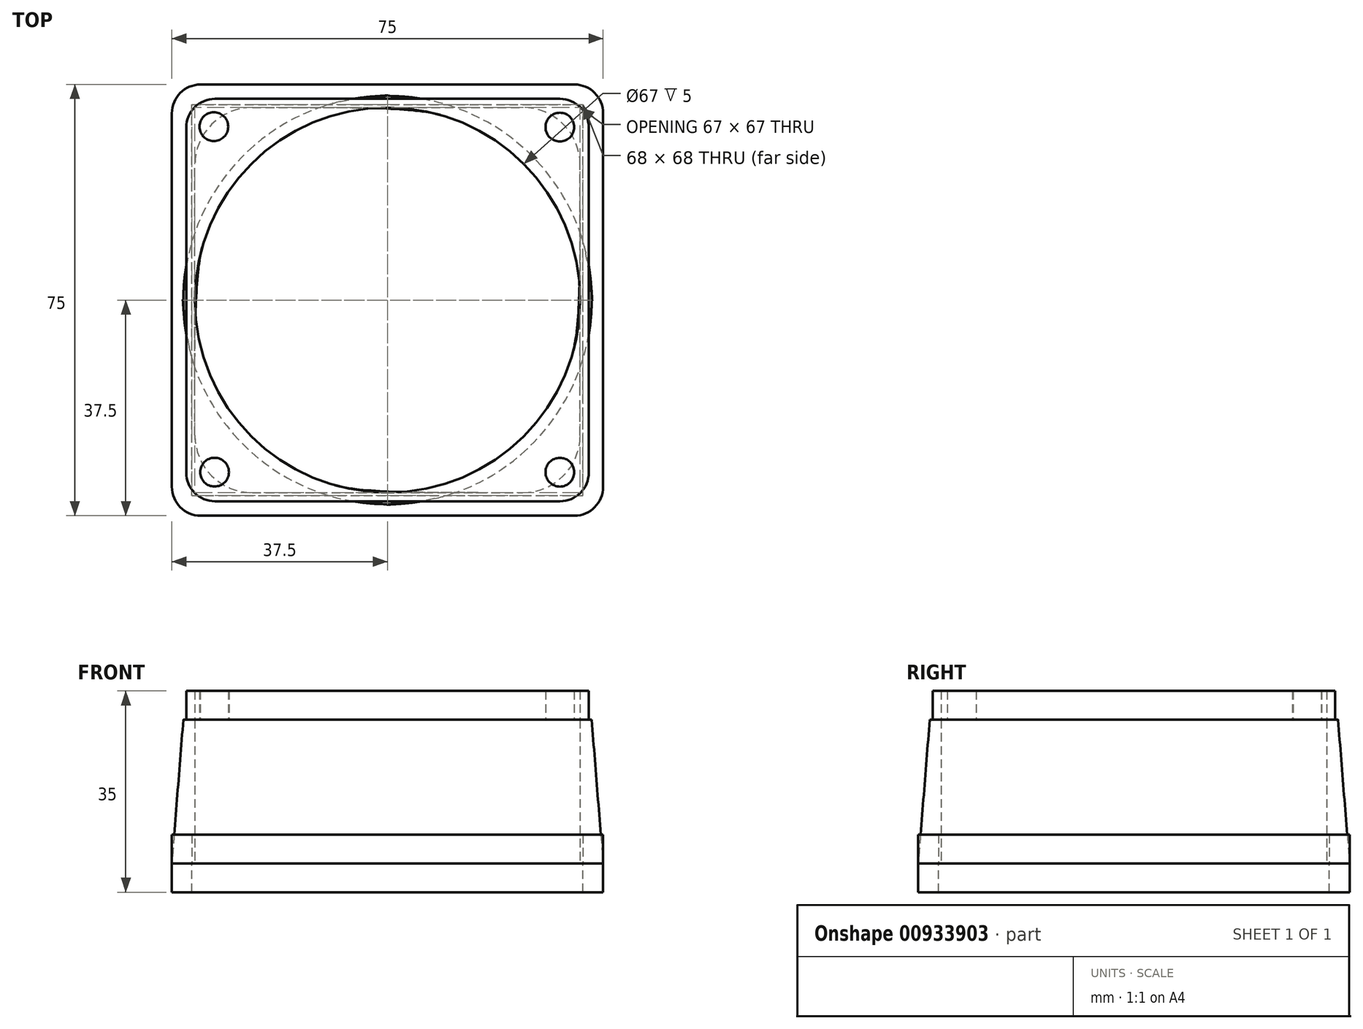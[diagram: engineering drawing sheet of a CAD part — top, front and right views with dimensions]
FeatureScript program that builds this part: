
annotation { "Feature Type Name" : "Feature", "Feature Type Description" : "" }
export const myFeature = defineFeature(function(context is Context, id is Id, definition is map)
    precondition{}
    {
        {
            var Q0;
            Q0=qCreatedBy(makeId("Top.planeOp"),FACE);
            cPlane(context, id + "F0", {"entities" : qUnion([Q0]), "cplaneType" : CPlaneType.OFFSET, "offset" : 25 * mm, "oppositeDirection" : true, "width" : 150 * mm, "height" : 150 * mm});
        }
        {
            var Q0;
            Q0=qCreatedBy(makeId("Top.planeOp"),FACE);
            var sketch = newSketch(context, id + "F1", { "sketchPlane" : qUnion([Q0])});
            skLineSegment(sketch, "E0.bottom", {"start": v(30, -35) * mm, "end": v(-30, -35) * mm});
            skLineSegment(sketch, "E0.top", {"start": v(30, 35) * mm, "end": v(-30, 35) * mm});
            skLineSegment(sketch, "E0.left", {"start": v(35, -30) * mm, "end": v(35, 30) * mm});
            skLineSegment(sketch, "E0.right", {"start": v(-35, -30) * mm, "end": v(-35, 30) * mm});
            skPoint(sketch, "E0.middle", {"position": v(0, 0) * mm});
            skPoint(sketch, "E1.visualSharp", {"position": v(35, -35) * mm});
            skArc(sketch, "E1.filletArc", {"start": v(30, -35) * mm, "mid": v(33.54, -33.54) * mm, "end": v(35, -30) * mm});
            skPoint(sketch, "E2.visualSharp", {"position": v(35, 35) * mm});
            skArc(sketch, "E2.filletArc", {"start": v(35, 30) * mm, "mid": v(33.54, 33.54) * mm, "end": v(30, 35) * mm});
            skPoint(sketch, "E3.visualSharp", {"position": v(-35, 35) * mm});
            skArc(sketch, "E3.filletArc", {"start": v(-30, 35) * mm, "mid": v(-33.54, 33.54) * mm, "end": v(-35, 30) * mm});
            skPoint(sketch, "E4.visualSharp", {"position": v(-35, -35) * mm});
            skArc(sketch, "E4.filletArc", {"start": v(-35, -30) * mm, "mid": v(-33.54, -33.54) * mm, "end": v(-30, -35) * mm});
            skSolve(sketch);
        }
        {
            var Q0;
            Q0=qCreatedBy(id+"F0.planeOp",FACE);
            var sketch = newSketch(context, id + "F2", { "sketchPlane" : qUnion([Q0])});
            skLineSegment(sketch, "E5.bottom", {"start": v(-23.5, -33.5) * mm, "end": v(23.5, -33.5) * mm});
            skLineSegment(sketch, "E5.top", {"start": v(-23.5, 33.5) * mm, "end": v(23.5, 33.5) * mm});
            skLineSegment(sketch, "E5.left", {"start": v(-33.5, -23.5) * mm, "end": v(-33.5, 23.5) * mm});
            skLineSegment(sketch, "E5.right", {"start": v(33.5, -23.5) * mm, "end": v(33.5, 23.5) * mm});
            skPoint(sketch, "E5.middle", {"position": v(0, 0) * mm});
            skPoint(sketch, "E6.visualSharp", {"position": v(-33.5, 33.5) * mm});
            skArc(sketch, "E6.filletArc", {"start": v(-23.5, 33.5) * mm, "mid": v(-30.57, 30.57) * mm, "end": v(-33.5, 23.5) * mm});
            skPoint(sketch, "E7.visualSharp", {"position": v(33.5, 33.5) * mm});
            skArc(sketch, "E7.filletArc", {"start": v(33.5, 23.5) * mm, "mid": v(30.57, 30.57) * mm, "end": v(23.5, 33.5) * mm});
            skPoint(sketch, "E8.visualSharp", {"position": v(33.5, -33.5) * mm});
            skArc(sketch, "E8.filletArc", {"start": v(23.5, -33.5) * mm, "mid": v(30.57, -30.57) * mm, "end": v(33.5, -23.5) * mm});
            skPoint(sketch, "E9.visualSharp", {"position": v(-33.5, -33.5) * mm});
            skArc(sketch, "E9.filletArc", {"start": v(-33.5, -23.5) * mm, "mid": v(-30.57, -30.57) * mm, "end": v(-23.5, -33.5) * mm});
            skSolve(sketch);
        }
        {
            var Q0;
            Q0=qCreatedBy(makeId("Top.planeOp"),FACE);
            var sketch = newSketch(context, id + "F3", { "sketchPlane" : qUnion([Q0])});
            skCircle(sketch, "E10", {"center": v(0, 0) * mm, "radius": 33.5 * mm});
            skSolve(sketch);
        }
        {
            var Q0;
            Q0=qCreatedBy(id+"F0.planeOp",FACE);
            var sketch = newSketch(context, id + "F4", { "sketchPlane" : qUnion([Q0])});
            skLineSegment(sketch, "E11.bottom", {"start": v(32.5, -37.5) * mm, "end": v(-32.5, -37.5) * mm});
            skLineSegment(sketch, "E11.top", {"start": v(32.5, 37.5) * mm, "end": v(-32.5, 37.5) * mm});
            skLineSegment(sketch, "E11.left", {"start": v(37.5, -32.5) * mm, "end": v(37.5, 32.5) * mm});
            skLineSegment(sketch, "E11.right", {"start": v(-37.5, -32.5) * mm, "end": v(-37.5, 32.5) * mm});
            skPoint(sketch, "E11.middle", {"position": v(0, 0) * mm});
            skPoint(sketch, "E12.visualSharp", {"position": v(37.5, -37.5) * mm});
            skArc(sketch, "E12.filletArc", {"start": v(32.5, -37.5) * mm, "mid": v(36.04, -36.04) * mm, "end": v(37.5, -32.5) * mm});
            skPoint(sketch, "E13.visualSharp", {"position": v(37.5, 37.5) * mm});
            skArc(sketch, "E13.filletArc", {"start": v(37.5, 32.5) * mm, "mid": v(36.04, 36.04) * mm, "end": v(32.5, 37.5) * mm});
            skPoint(sketch, "E14.visualSharp", {"position": v(-37.5, 37.5) * mm});
            skArc(sketch, "E14.filletArc", {"start": v(-32.5, 37.5) * mm, "mid": v(-36.04, 36.04) * mm, "end": v(-37.5, 32.5) * mm});
            skPoint(sketch, "E15.visualSharp", {"position": v(-37.5, -37.5) * mm});
            skArc(sketch, "E15.filletArc", {"start": v(-37.5, -32.5) * mm, "mid": v(-36.04, -36.04) * mm, "end": v(-32.5, -37.5) * mm});
            skSolve(sketch);
        }
        {
            var Q0;
            Q0=qCreatedBy(makeId("Top.planeOp"),FACE);
            var sketch = newSketch(context, id + "F5", { "sketchPlane" : qUnion([Q0])});
            skCircle(sketch, "E16", {"center": v(0, 0) * mm, "radius": 35.5 * mm});
            skSolve(sketch);
        }
        {
            var Q0;
            Q0=qCreatedBy(id+"F0.planeOp",FACE);
            var sketch = newSketch(context, id + "F6", { "sketchPlane" : qUnion([Q0])});
            skLineSegment(sketch, "E17.bottom", {"start": v(-34, -34) * mm, "end": v(34, -34) * mm});
            skLineSegment(sketch, "E17.top", {"start": v(-34, 34) * mm, "end": v(34, 34) * mm});
            skLineSegment(sketch, "E17.left", {"start": v(-34, -34) * mm, "end": v(-34, 34) * mm});
            skLineSegment(sketch, "E17.right", {"start": v(34, -34) * mm, "end": v(34, 34) * mm});
            skPoint(sketch, "E17.middle", {"position": v(0, 0) * mm});
            skSolve(sketch);
        }
        {
            var Q0;
            Q0 = qSketchRegion(id + "F8", true);
            var Q1;
            Q1 = qSketchRegion(id + "F1", true);
            extrude(context, id + "F7", {"entities" : qUnion([Q0, Q1]), "depth" : 5 * mm, "offsetDistance" : 25 * mm});
        }
        {
            var Q0;
            Q0=qCreatedBy(makeId("Top.planeOp"),FACE);
            var sketch = newSketch(context, id + "F8", { "sketchPlane" : qUnion([Q0])});
            skCircle(sketch, "E18", {"center": v(-30.2, 30.16) * mm, "radius": 2.5 * mm});
            skCircle(sketch, "E19", {"center": v(29.97, 30.09) * mm, "radius": 2.5 * mm});
            skCircle(sketch, "E20", {"center": v(29.97, -29.94) * mm, "radius": 2.5 * mm});
            skCircle(sketch, "E21", {"center": v(-30.08, -29.93) * mm, "radius": 2.5 * mm});
            skSolve(sketch);
        }
        {
            var Q0;
            Q0 = qSketchRegion(id + "F3", true);
            var Q1;
            Q1 = qSketchRegion(id + "F6", true);
            var Q2;
            Q2 = qSketchRegion(id + "F4", true);
            extrude(context, id + "F9", {"entities" : qUnion([Q0, Q1, Q2]), "depth" : 5 * mm, "offsetDistance" : 25 * mm});
        }
        {
            var Q0;
            Q0 = qSketchRegion(id + "F8", true);
            extrude(context, id + "F10", {"entities" : qUnion([Q0]), "depth" : 5 * mm, "offsetDistance" : 25 * mm});
        }
        {
            var Q0;
            Q0=makeQuery(id+"F9.opExtrude","SWEPT_BODY",BODY,{"disambiguationData":[OSD([sQuery(id+"F3.wireOp",EDGE,"E10")])]});
            var Q1;
            Q1=makeQuery(id+"F10.opExtrude","SWEPT_BODY",BODY,{"disambiguationData":[OSD([sQuery(id+"F8.wireOp",EDGE,"E19")])]});
            var Q2;
            Q2=makeQuery(id+"F10.opExtrude","SWEPT_BODY",BODY,{"disambiguationData":[OSD([sQuery(id+"F8.wireOp",EDGE,"E21")])]});
            var Q3;
            Q3=makeQuery(id+"F10.opExtrude","SWEPT_BODY",BODY,{"disambiguationData":[OSD([sQuery(id+"F8.wireOp",EDGE,"E18")])]});
            var Q4;
            Q4=makeQuery(id+"F10.opExtrude","SWEPT_BODY",BODY,{"disambiguationData":[OSD([sQuery(id+"F8.wireOp",EDGE,"E20")])]});
            var Q5;
            Q5=makeQuery(id+"F7.opExtrude","SWEPT_BODY",BODY,{"disambiguationData":[OSD([sQuery(id+"F1.wireOp",EDGE,"E0.bottom"),sQuery(id+"F1.wireOp",EDGE,"E0.top"),sQuery(id+"F1.wireOp",EDGE,"E0.left"),sQuery(id+"F1.wireOp",EDGE,"E0.right"),sQuery(id+"F1.wireOp",EDGE,"E1.filletArc"),sQuery(id+"F1.wireOp",EDGE,"E2.filletArc"),sQuery(id+"F1.wireOp",EDGE,"E3.filletArc"),sQuery(id+"F1.wireOp",EDGE,"E4.filletArc")])]});
            booleanBodies(context, id + "F11", {"operationType" : BooleanOperationType.SUBTRACTION, "tools" : qUnion([Q0, Q1, Q2, Q3, Q4]), "targets" : qUnion([Q5])});
        }
        {
            var Q0;
            Q0 = qSketchRegion(id + "F3", true);
            var Q1;
            Q1 = qSketchRegion(id + "F2", true);
            loft(context, id + "F12", {"sheetProfilesArray" : [{ "sheetProfileEntities" : qUnion([Q0]) }, { "sheetProfileEntities" : qUnion([Q1]) }]});
        }
        {
            var Q0;
            Q0 = qSketchRegion(id + "F5", true);
            var Q1;
            Q1 = qSketchRegion(id + "F4", true);
            loft(context, id + "F13", {"sheetProfilesArray" : [{ "sheetProfileEntities" : qUnion([Q0]) }, { "sheetProfileEntities" : qUnion([Q1]) }]});
        }
        {
            var Q0;
            Q0=makeQuery(id+"F12.opLoft","SWEPT_BODY",BODY,{"disambiguationData":[OSD([makeQuery(id+"F2.imprint","IMPRINT",FACE,{"disambiguationData":[TD([[makeQuery(id+"F2.imprint","IMPRINT",EDGE,{"derivedFrom":sQuery(id+"F2.wireOp",EDGE,"E5.bottom")}),1.0]])]}),makeQuery(id+"F3.imprint","IMPRINT",FACE,{"disambiguationData":[TD([[makeQuery(id+"F3.imprint","IMPRINT",EDGE,{"derivedFrom":sQuery(id+"F3.wireOp",EDGE,"E10")}),1.0]])]})])]});
            var Q1;
            Q1=makeQuery(id+"F13.opLoft","SWEPT_BODY",BODY,{"disambiguationData":[OSD([makeQuery(id+"F4.imprint","IMPRINT",FACE,{"disambiguationData":[TD([[makeQuery(id+"F4.imprint","IMPRINT",EDGE,{"derivedFrom":sQuery(id+"F4.wireOp",EDGE,"E11.bottom")}),-1.0]])]}),makeQuery(id+"F5.imprint","IMPRINT",FACE,{"disambiguationData":[TD([[makeQuery(id+"F5.imprint","IMPRINT",EDGE,{"derivedFrom":sQuery(id+"F5.wireOp",EDGE,"E16")}),1.0]])]})])]});
            booleanBodies(context, id + "F14", {"operationType" : BooleanOperationType.SUBTRACTION, "tools" : qUnion([Q0]), "targets" : qUnion([Q1])});
        }
        {
            var Q0;
            Q0=makeQuery(id+"F4.imprint","IMPRINT",FACE,{"disambiguationData":[TD([[makeQuery(id+"F4.imprint","IMPRINT",EDGE,{"derivedFrom":sQuery(id+"F4.wireOp",EDGE,"E11.bottom")}),-1.0]])]});
            extrude(context, id + "F15", {"entities" : qUnion([Q0]), "oppositeDirection" : true, "depth" : 5 * mm, "offsetDistance" : 25 * mm});
        }
        {
            var Q0;
            Q0 = qSketchRegion(id + "F6", true);
            extrude(context, id + "F16", {"entities" : qUnion([Q0]), "oppositeDirection" : true, "depth" : 10 * mm, "offsetDistance" : 25 * mm});
        }
        {
            var Q0;
            Q0=makeQuery(id+"F16.opExtrude","SWEPT_BODY",BODY,{"disambiguationData":[OSD([sQuery(id+"F6.wireOp",EDGE,"E17.bottom"),sQuery(id+"F6.wireOp",EDGE,"E17.top"),sQuery(id+"F6.wireOp",EDGE,"E17.left"),sQuery(id+"F6.wireOp",EDGE,"E17.right")])]});
            var Q1;
            Q1=makeQuery(id+"F15.opExtrude","SWEPT_BODY",BODY,{"disambiguationData":[OSD([sQuery(id+"F4.wireOp",EDGE,"E11.bottom"),sQuery(id+"F4.wireOp",EDGE,"E11.top"),sQuery(id+"F4.wireOp",EDGE,"E11.left"),sQuery(id+"F4.wireOp",EDGE,"E11.right"),sQuery(id+"F4.wireOp",EDGE,"E12.filletArc"),sQuery(id+"F4.wireOp",EDGE,"E13.filletArc"),sQuery(id+"F4.wireOp",EDGE,"E14.filletArc"),sQuery(id+"F4.wireOp",EDGE,"E15.filletArc")])]});
            booleanBodies(context, id + "F17", {"operationType" : BooleanOperationType.SUBTRACTION, "tools" : qUnion([Q0]), "targets" : qUnion([Q1])});
        }
    });
